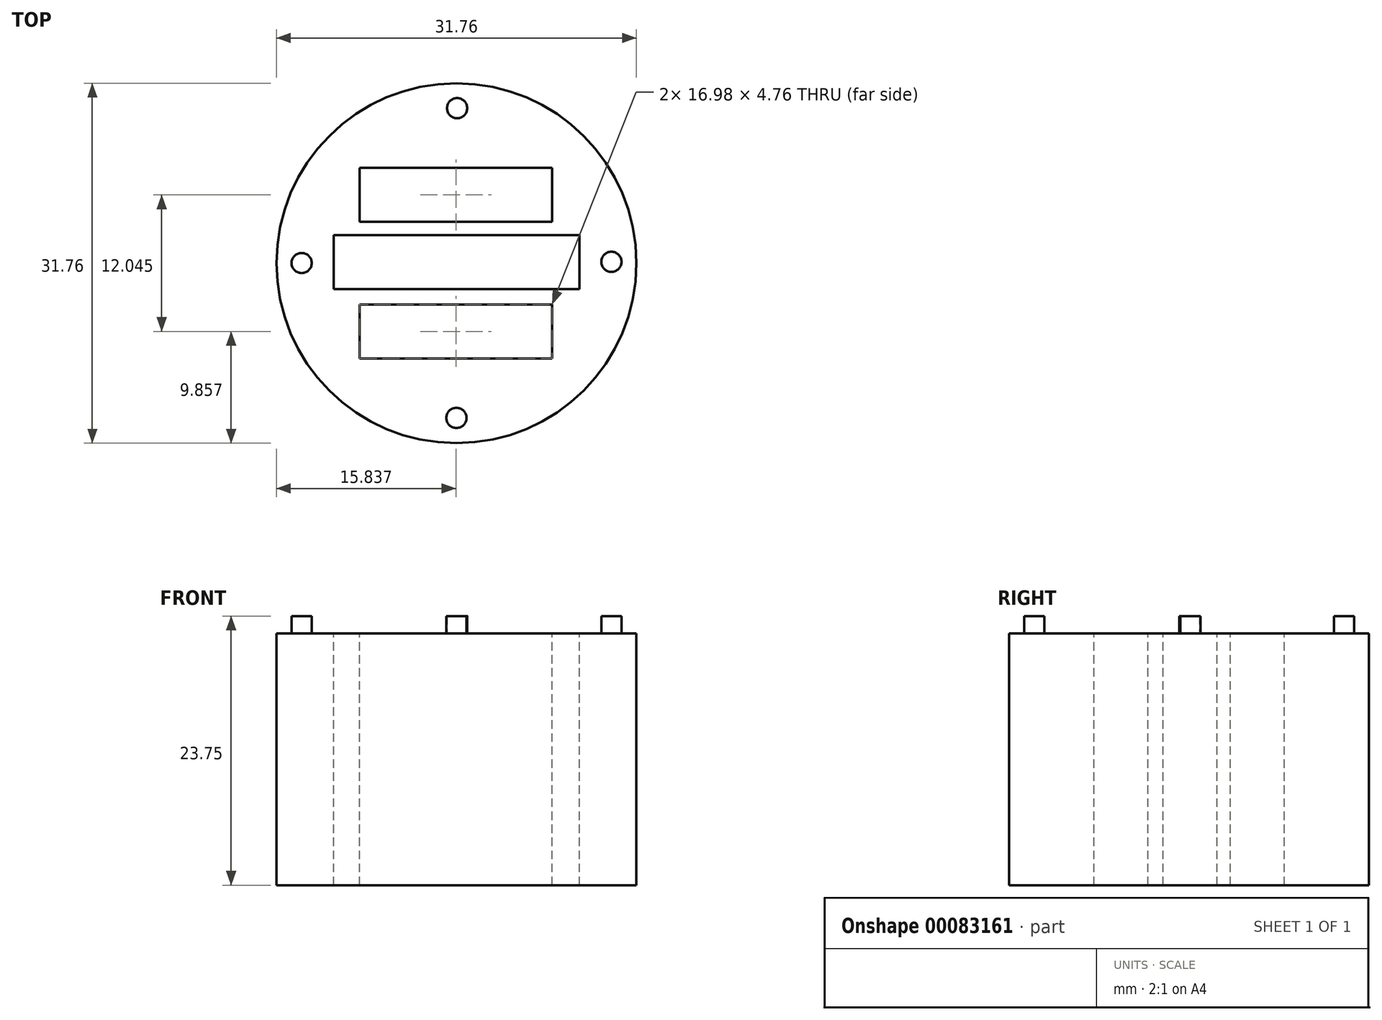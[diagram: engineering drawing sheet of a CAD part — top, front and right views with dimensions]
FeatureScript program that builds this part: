
annotation { "Feature Type Name" : "Feature", "Feature Type Description" : "" }
export const myFeature = defineFeature(function(context is Context, id is Id, definition is map)
    precondition{}
    {
        {
            var Q0;
            Q0=qCreatedBy(makeId("Top.planeOp"),FACE);
            var sketch = newSketch(context, id + "F0", { "sketchPlane" : qUnion([Q0])});
            skCircle(sketch, "E0", {"center": v(0, 0) * mm, "radius": 15.88 * mm});
            skSolve(sketch);
        }
        {
            var Q0;
            Q0=qSketchRegion(id+"F0",true);
            extrude(context, id + "F1", {"entities" : qUnion([Q0]), "depth" : 22.22 * mm});
        }
        {
            var Q0;
            Q0=makeQuery(id+"F1.opExtrude","CAP_FACE",FACE,{"disambiguationData":[OSD([sQuery(id+"F0.wireOp",EDGE,"E0")])],"isStart":true});
            var sketch = newSketch(context, id + "F2", { "sketchPlane" : qUnion([Q0])});
            skCircle(sketch, "E1", {"center": v(0, 0) * mm, "radius": 12.7 * mm});
            skSolve(sketch);
        }
        {
            var Q0;
            Q0=makeQuery(id+"F2.imprint","IMPRINT",FACE,{"disambiguationData":[TD([[makeQuery(id+"F2.imprint","IMPRINT",EDGE,{"derivedFrom":sQuery(id+"F2.wireOp",EDGE,"E1")}),-1.0]])]});
            var sketch = newSketch(context, id + "F3", { "sketchPlane" : qUnion([Q0])});
            skCircle(sketch, "E2", {"center": v(0, 13.65) * mm, "radius": 0.89 * mm});
            skCircle(sketch, "E3", {"center": v(-13.66, -0.02) * mm, "radius": 0.89 * mm});
            skCircle(sketch, "E4", {"center": v(0.06, -13.68) * mm, "radius": 0.89 * mm});
            skCircle(sketch, "E5", {"center": v(13.67, -0.12) * mm, "radius": 0.89 * mm});
            skSolve(sketch);
        }
        {
            var Q0;
            Q0=makeQuery(id+"F1.opExtrude","CAP_FACE",FACE,{"disambiguationData":[OSD([sQuery(id+"F0.wireOp",EDGE,"E0")])],"isStart":false});
            var sketch = newSketch(context, id + "F4", { "sketchPlane" : qUnion([Q0])});
            skCircle(sketch, "E6", {"center": v(0, 0) * mm, "radius": 11.35 * mm});
            skSolve(sketch);
        }
        {
            var Q0;
            Q0=qSketchRegion(id+"F3",true);
            extrude(context, id + "F5", {"entities" : qUnion([Q0]), "operationType" : NewBodyOperationType.ADD, "oppositeDirection" : true, "depth" : 23.75 * mm});
        }
        {
            var Q0;
            Q0=makeQuery(id+"F4.imprint","IMPRINT",FACE,{"disambiguationData":[TD([[makeQuery(id+"F4.imprint","IMPRINT",EDGE,{"derivedFrom":sQuery(id+"F4.wireOp",EDGE,"E6")}),-1.0]])]});
            var sketch = newSketch(context, id + "F9", { "sketchPlane" : qUnion([Q0])});
            skLineSegment(sketch, "E7.bottom", {"start": v(-10.84, 2.48) * mm, "end": v(10.87, 2.48) * mm});
            skLineSegment(sketch, "E7.top", {"start": v(-10.84, -2.28) * mm, "end": v(10.87, -2.28) * mm});
            skLineSegment(sketch, "E7.left", {"start": v(-10.84, 2.48) * mm, "end": v(-10.84, -2.28) * mm});
            skLineSegment(sketch, "E7.right", {"start": v(10.87, 2.48) * mm, "end": v(10.87, -2.28) * mm});
            skSolve(sketch);
        }
        {
            var Q0;
            Q0=makeQuery(id+"F9.imprint","IMPRINT",FACE,{"disambiguationData":[TD([[makeQuery(id+"F9.imprint","IMPRINT",EDGE,{"derivedFrom":makeQuery(id+"F4.imprint","IMPRINT",EDGE,{"derivedFrom":sQuery(id+"F4.wireOp",EDGE,"E6")})}),-1.0]])]});
            var sketch = newSketch(context, id + "F6", { "sketchPlane" : qUnion([Q0])});
            skLineSegment(sketch, "E8.bottom", {"start": v(-8.53, 8.4) * mm, "end": v(8.45, 8.4) * mm});
            skLineSegment(sketch, "E8.top", {"start": v(-8.53, 3.64) * mm, "end": v(8.45, 3.64) * mm});
            skLineSegment(sketch, "E8.left", {"start": v(-8.53, 8.4) * mm, "end": v(-8.53, 3.64) * mm});
            skLineSegment(sketch, "E8.right", {"start": v(8.45, 8.4) * mm, "end": v(8.45, 3.64) * mm});
            skLineSegment(sketch, "E9.MirrorCS", {"start": v(-8.53, -8.4) * mm, "end": v(-8.53, -3.64) * mm});
            skLineSegment(sketch, "E10.MirrorCS", {"start": v(8.45, -8.4) * mm, "end": v(8.45, -3.64) * mm});
            skLineSegment(sketch, "E11.MirrorCS", {"start": v(-8.53, -8.4) * mm, "end": v(8.45, -8.4) * mm});
            skLineSegment(sketch, "E12.MirrorCS", {"start": v(-8.53, -3.64) * mm, "end": v(8.45, -3.64) * mm});
            skSolve(sketch);
        }
        {
            var Q0;
            Q0 = qSketchRegion(id + "F9", true);
            extrude(context, id + "F7", {"entities" : qUnion([Q0]), "operationType" : NewBodyOperationType.REMOVE, "oppositeDirection" : true, "depth" : 22.22 * mm});
        }
        {
            var Q0;
            Q0 = qSketchRegion(id + "F6", true);
            extrude(context, id + "F8", {"entities" : qUnion([Q0]), "operationType" : NewBodyOperationType.REMOVE, "oppositeDirection" : true, "depth" : 22.22 * mm});
        }
    });
